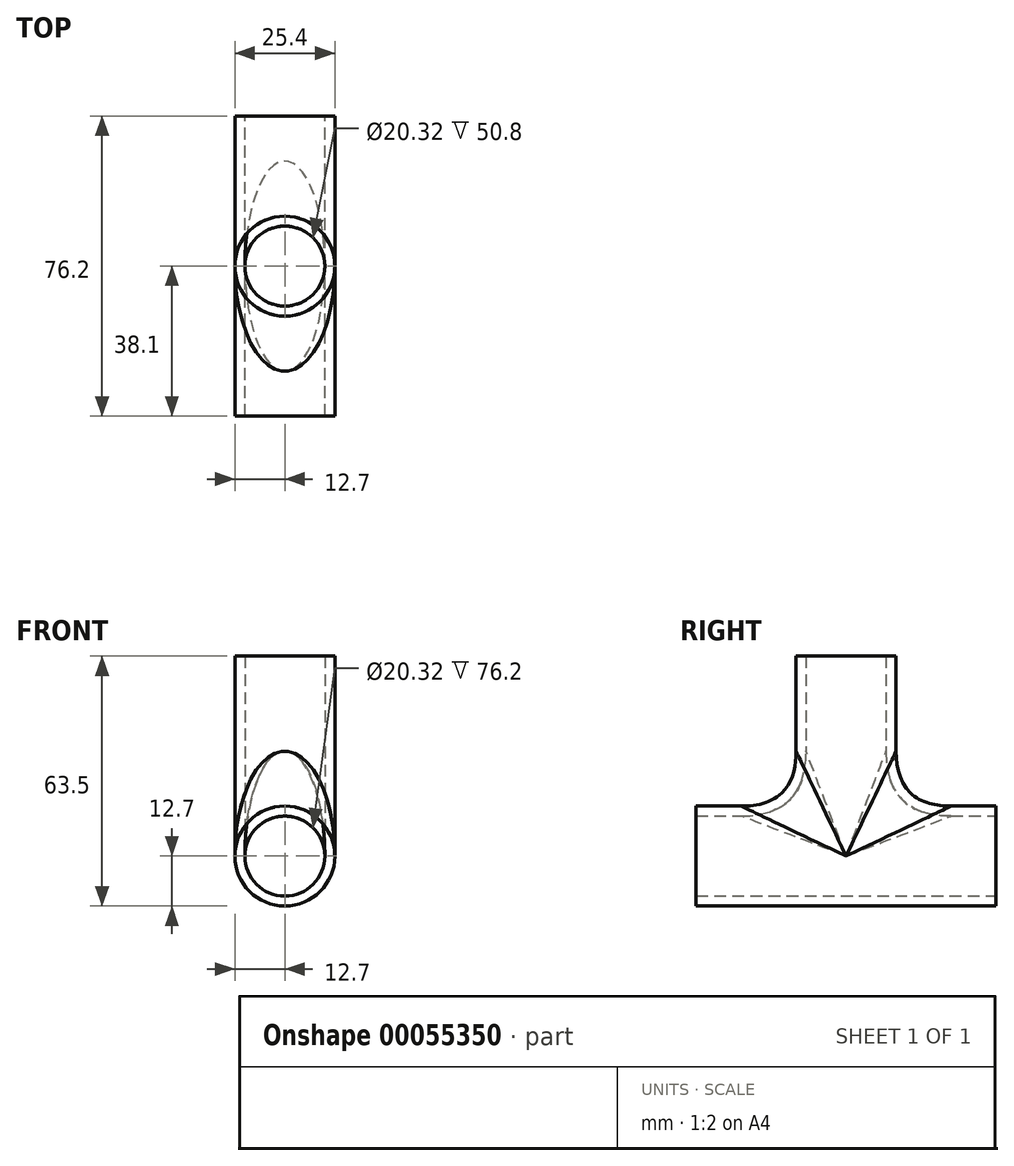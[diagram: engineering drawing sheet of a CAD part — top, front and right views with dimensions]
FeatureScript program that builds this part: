
annotation { "Feature Type Name" : "Feature", "Feature Type Description" : "" }
export const myFeature = defineFeature(function(context is Context, id is Id, definition is map)
    precondition{}
    {
        {
            var Q0;
            Q0=qCreatedBy(makeId("Front.planeOp"),FACE);
            var sketch = newSketch(context, id + "F0", { "sketchPlane" : qUnion([Q0])});
            skCircle(sketch, "E0", {"center": v(0, 0) * mm, "radius": 12.7 * mm});
            skCircle(sketch, "E1", {"center": v(0, 0) * mm, "radius": 10.16 * mm});
            skSolve(sketch);
        }
        {
            var Q0;
            Q0 = qSketchRegion(id + "F0", true);
            extrude(context, id + "F1", {"entities" : qUnion([Q0]), "endBound" : BoundingType.SYMMETRIC, "depth" : 76.2 * mm, "hasSecondDirection" : true, "secondDirectionOppositeDirection" : true, "secondDirectionDepth" : 25.4 * mm});
        }
        {
            var Q0;
            Q0=qCreatedBy(makeId("Top.planeOp"),FACE);
            var sketch = newSketch(context, id + "F2", { "sketchPlane" : qUnion([Q0])});
            skCircle(sketch, "E2", {"center": v(0, 0) * mm, "radius": 10.16 * mm});
            skSolve(sketch);
        }
        {
            var Q0;
            Q0=makeQuery(id+"F2.imprint","IMPRINT",FACE,{"disambiguationData":[TD([[makeQuery(id+"F2.imprint","IMPRINT",EDGE,{"derivedFrom":sQuery(id+"F2.wireOp",EDGE,"E2")}),1.0]])]});
            var Q1;
            Q1=sQuery(id+"F2.wireOp",EDGE,"E2");
            extrude(context, id + "F3", {"entities" : qUnion([Q0]), "operationType" : NewBodyOperationType.REMOVE, "surfaceEntities" : qUnion([Q1]), "depth" : 25.4 * mm});
        }
        {
            var Q0;
            Q0=qCreatedBy(makeId("Top.planeOp"),FACE);
            var sketch = newSketch(context, id + "F4", { "sketchPlane" : qUnion([Q0])});
            skCircle(sketch, "E3", {"center": v(0, 0) * mm, "radius": 12.7 * mm});
            skCircle(sketch, "E4", {"center": v(0, 0) * mm, "radius": 10.16 * mm});
            skSolve(sketch);
        }
        {
            var Q0;
            Q0 = qSketchRegion(id + "F4", true);
            extrude(context, id + "F5", {"entities" : qUnion([Q0]), "operationType" : NewBodyOperationType.ADD, "depth" : 50.8 * mm});
        }
        {
            var Q0;
            Q0=qCreatedBy(makeId("Front.planeOp"),FACE);
            var sketch = newSketch(context, id + "F6", { "sketchPlane" : qUnion([Q0])});
            skCircle(sketch, "E5", {"center": v(0, 0) * mm, "radius": 10.16 * mm});
            skSolve(sketch);
        }
        {
            var Q0;
            Q0 = qSketchRegion(id + "F6", true);
            extrude(context, id + "F7", {"entities" : qUnion([Q0]), "operationType" : NewBodyOperationType.REMOVE, "endBound" : BoundingType.SYMMETRIC, "oppositeDirection" : true, "depth" : 25.4 * mm});
        }
        {
            var Q0;
            Q0=makeQuery(id+"F5.boolean.opBoolean","INTERSECT",EDGE,{"disambiguationData":[OD(0.0)],"derivedFrom":[makeQuery(id+"F1.opExtrude","SWEPT_FACE",FACE,{"disambiguationData":[OSD([sQuery(id+"F0.wireOp",EDGE,"E0")])]}),makeQuery(id+"F5.opExtrude","SWEPT_FACE",FACE,{"disambiguationData":[OSD([sQuery(id+"F4.wireOp",EDGE,"E3")])]})]});
            var Q1;
            Q1=makeQuery(id+"F5.boolean.opBoolean","INTERSECT",EDGE,{"disambiguationData":[OD(1.0)],"derivedFrom":[makeQuery(id+"F1.opExtrude","SWEPT_FACE",FACE,{"disambiguationData":[OSD([sQuery(id+"F0.wireOp",EDGE,"E0")])]}),makeQuery(id+"F5.opExtrude","SWEPT_FACE",FACE,{"disambiguationData":[OSD([sQuery(id+"F4.wireOp",EDGE,"E3")])]})]});
            fillet(context, id + "F8", {"entities" : qUnion([Q0, Q1]), "radius" : 13.97 * mm, "tangentPropagation" : true, "rho" : 0.5, "crossSection" : FilletCrossSection.CONIC, "allowEdgeOverflow" : false});
        }
        {
            var Q0;
            Q0=makeQuery(id+"F7.boolean.opBoolean","INTERSECT",EDGE,{"disambiguationData":[OD(1.0)],"derivedFrom":[makeQuery(id+"F5.boolean.opBoolean","MERGE",FACE,{"derivedFrom":[makeQuery(id+"F3.boolean.opBoolean","COPY",FACE,{"derivedFrom":makeQuery(id+"F3.opExtrude","SWEPT_FACE",FACE,{"disambiguationData":[OSD([sQuery(id+"F2.wireOp",EDGE,"E2")])]})}),makeQuery(id+"F5.opExtrude","SWEPT_FACE",FACE,{"disambiguationData":[OSD([sQuery(id+"F4.wireOp",EDGE,"E4")])]})]}),makeQuery(id+"F7.opExtrude","SWEPT_FACE",FACE,{"disambiguationData":[OSD([sQuery(id+"F6.wireOp",EDGE,"E5")])]})]});
            var Q1;
            Q1=makeQuery(id+"F7.boolean.opBoolean","INTERSECT",EDGE,{"disambiguationData":[OD(0.0)],"derivedFrom":[makeQuery(id+"F5.boolean.opBoolean","MERGE",FACE,{"derivedFrom":[makeQuery(id+"F3.boolean.opBoolean","COPY",FACE,{"derivedFrom":makeQuery(id+"F3.opExtrude","SWEPT_FACE",FACE,{"disambiguationData":[OSD([sQuery(id+"F2.wireOp",EDGE,"E2")])]})}),makeQuery(id+"F5.opExtrude","SWEPT_FACE",FACE,{"disambiguationData":[OSD([sQuery(id+"F4.wireOp",EDGE,"E4")])]})]}),makeQuery(id+"F7.opExtrude","SWEPT_FACE",FACE,{"disambiguationData":[OSD([sQuery(id+"F6.wireOp",EDGE,"E5")])]})]});
            fillet(context, id + "F9", {"entities" : qUnion([Q0, Q1]), "radius" : 16.5 * mm, "tangentPropagation" : true, "rho" : 0.5, "crossSection" : FilletCrossSection.CONIC, "allowEdgeOverflow" : false});
        }
    });
